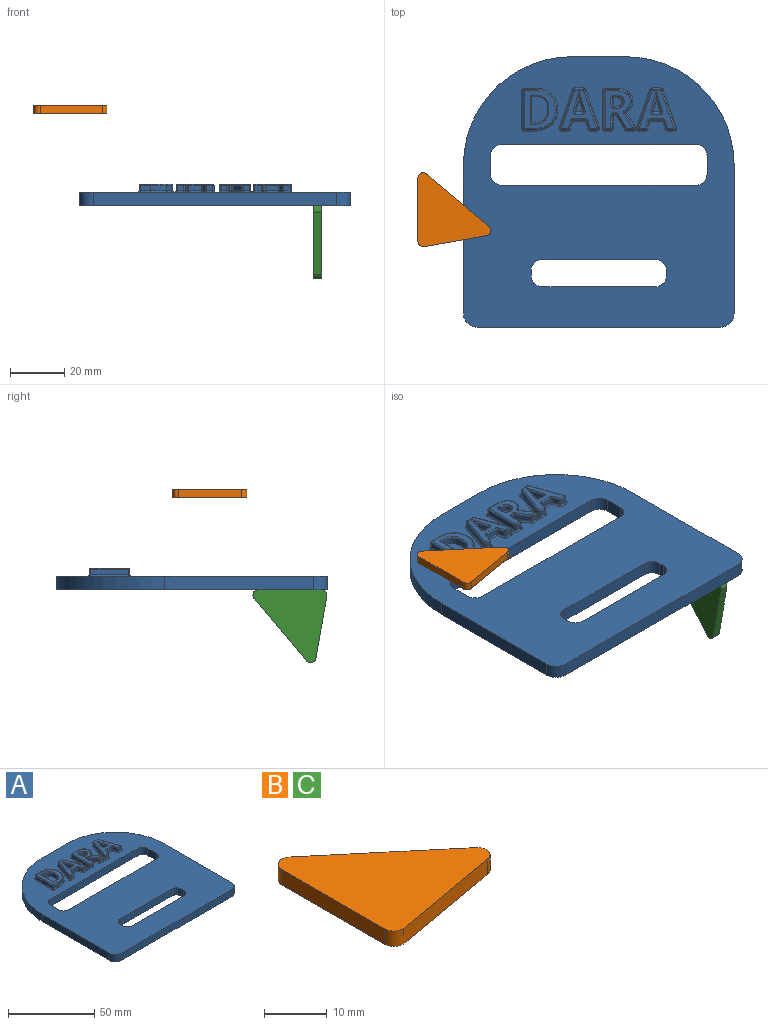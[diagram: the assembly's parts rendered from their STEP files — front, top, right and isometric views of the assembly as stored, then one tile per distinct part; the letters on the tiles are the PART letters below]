
ASSEMBLY  parts=3 mates=1
PART A: 298 faces, bbox 100x100x8 mm
  f0: plane 100x100mm, normal (0,0,1), area 7009.5mm2, adj f1,f2,f3,f4,f5,f6,f7,f8
  f1: plane 20x5mm, normal (0,1,0), area 100mm2, adj f0,f2,f24,f25
  f2: cylinder r=40mm len=40mm, axis (0,0,-1), area 314.2mm2, adj f0,f1,f3,f25
  f3: plane 55x5mm, normal (-1,0,0), area 275mm2, adj f0,f2,f4,f25
  f4: cylinder r=5mm len=5mm, axis (0,0,-1), area 39.3mm2, adj f0,f3,f5,f25
  f5: plane 90x5mm, normal (0,-1,0), area 450mm2, adj f0,f4,f6,f25
  f6: cylinder r=5mm len=5mm, axis (0,0,-1), area 39.3mm2, adj f0,f5,f7,f25
  f7: plane 55x5mm, normal (1,0,0), area 275mm2, adj f0,f6,f24,f25
  f8: cylinder r=4mm len=5mm, axis (0,0,-1), area 31.4mm2, adj f0,f9,f22,f25
  f9: plane 72x5mm, normal (0,-1,0), area 360mm2, adj f0,f8,f10,f25
  f10: cylinder r=4mm len=5mm, axis (0,0,-1), area 31.4mm2, adj f0,f9,f11,f25
  f11: plane 7x5mm, normal (-1,0,0), area 35mm2, adj f0,f10,f12,f25
  f12: cylinder r=4mm len=5mm, axis (0,0,-1), area 31.4mm2, adj f0,f11,f13,f25
  f13: plane 72x5mm, normal (0,1,0), area 360mm2, adj f0,f12,f14,f25
  f14: cylinder r=4mm len=5mm, axis (0,0,-1), area 31.4mm2, adj f0,f13,f22,f25
  f15: cylinder r=4mm len=5mm, axis (0,0,-1), area 31.4mm2, adj f0,f16,f23,f25
  f16: plane 5x2mm, normal (1,0,0), area 10mm2, adj f0,f15,f17,f25
  f17: cylinder r=4mm len=5mm, axis (0,0,-1), area 31.4mm2, adj f0,f16,f18,f25
  f18: plane 42x5mm, normal (0,-1,0), area 210mm2, adj f0,f17,f19,f25
  f19: cylinder r=4mm len=5mm, axis (0,0,-1), area 31.4mm2, adj f0,f18,f20,f25
  f20: plane 5x2mm, normal (-1,0,0), area 10mm2, adj f0,f19,f21,f25
  f21: cylinder r=4mm len=5mm, axis (0,0,-1), area 31.4mm2, adj f0,f20,f23,f25
  f22: plane 7x5mm, normal (1,0,0), area 35mm2, adj f0,f8,f14,f25
  f23: plane 42x5mm, normal (0,1,0), area 210mm2, adj f0,f15,f21,f25
  f24: cylinder r=40mm len=40mm, axis (0,0,-1), area 314.2mm2, adj f0,f1,f7,f25
  f25: plane 100x100mm, normal (0,0,-1), area 7630mm2, adj f1,f2,f3,f4,f5,f6,f7,f8
  f26: extruded ~4.79x4.23mm, area 18.3mm2, adj f27,f37,f39,f112
  f27: extruded ~4.89x4.56mm, area 19.2mm2, adj f26,f28,f39,f113
  f28: plane 2.5x1.35mm, normal (0,1,0), area 3.4mm2, adj f27,f29,f39,f111
  f29: plane 9.68x2.5mm, normal (1,0,0), area 24.2mm2, adj f28,f37,f39,f109
  f30: extruded ~5.63x2.09mm, area 12.4mm2, adj f31,f36,f91,f108
  f31: extruded ~5.37x2.02mm, area 11.8mm2, adj f30,f32,f89,f106
  f32: extruded ~5.66x2mm, area 12.3mm2, adj f31,f33,f90,f104
  f33: plane 4.17x2mm, normal (0,1,0), area 8.3mm2, adj f32,f92,f97,f102
  f34: plane 13.87x2mm, normal (-1,0,0), area 27.7mm2, adj f95,f97,f100,f101
  f35: plane 3.71x2mm, normal (0,-1,0), area 7.4mm2, adj f36,f96,f101,f105
  f36: extruded ~6.04x2mm, area 13mm2, adj f30,f35,f93,f107
  f37: plane 2.5x1.68mm, normal (0,-1,0), area 4.2mm2, adj f26,f29,f39,f110
  f38: plane 13.87x11.34mm, normal (0,0,1), area 74.5mm2, adj f89,f90,f91,f92,f93,f95,f96,f109
  f39: plane 9.68x5.91mm, normal (0,0,1), area 50.1mm2, adj f26,f27,f28,f29,f37
  f40: extruded ~4.79x2mm, area 10mm2, adj f51,f115,f119,f132
  f41: plane 2.52x2mm, normal (0,1,0), area 5mm2, adj f118,f119,f124,f130
  f42: extruded ~5.42x2mm, area 11.3mm2, adj f117,f124,f139,f295
  f43: plane 2.83x2mm, normal (-0.96,-0.29,0), area 5.9mm2, adj f141,f142,f150,f151
  f44: plane 2.32x2mm, normal (0,-1,0), area 4.6mm2, adj f126,f127,f140,f141
  f45: plane 13.94x4.92mm, normal (0.94,0.33,0), area 29.6mm2, adj f120,f126,f129,f131
  f46: plane 3.15x2mm, normal (0,1,0), area 6.3mm2, adj f128,f129,f144,f145
  f47: plane 13.94x4.9mm, normal (-0.94,0.33,0), area 29.5mm2, adj f143,f144,f155,f156
  f48: plane 2.32x2mm, normal (0,-1,0), area 4.6mm2, adj f154,f155,f163,f164
  f49: plane 2.83x2mm, normal (0.96,-0.29,0), area 5.9mm2, adj f153,f162,f163,f167
  f50: plane 4.68x2mm, normal (0,-1,0), area 9.4mm2, adj f151,f152,f161,f162
  f51: extruded ~2x0.62mm, area 1.3mm2, adj f40,f114,f138,f295
  f52: plane 13.94x12.96mm, normal (0,0,1), area 65.1mm2, adj f123,f130,f131,f132,f133,f138,f139,f140
  f53: plane 4.11x2.52mm, normal (0,0,1), area 5.2mm2, adj f115,f117,f118
  f54: plane 4.71x2mm, normal (1,0,0), area 9.4mm2, adj f181,f182,f192,f193
  f55: plane 2x0.9mm, normal (0,-1,0), area 1.8mm2, adj f171,f172,f180,f181
  f56: plane 5.23x3.26mm, normal (-0.85,-0.53,0), area 12.3mm2, adj f168,f171,f174,f175
  f57: plane 2.27x2mm, normal (0,-1,0), area 4.5mm2, adj f173,f174,f185,f186
  f58: extruded ~5.23x3.52mm, area 12.6mm2, adj f184,f185,f196,f197
  f59: extruded ~2x1.55mm, area 4.2mm2, adj f60,f183,f196,f206
  f60: extruded ~2.33x2mm, area 5mm2, adj f59,f61,f189,f209
  f61: extruded ~3.35x2mm, area 7.6mm2, adj f60,f62,f195,f212
  f62: extruded ~4.49x2mm, area 9.4mm2, adj f61,f63,f200,f214
  f63: plane 3.83x2mm, normal (0,1,0), area 7.7mm2, adj f62,f205,f211,f215
  f64: plane 13.87x2mm, normal (-1,0,0), area 27.7mm2, adj f203,f204,f210,f211
  f65: plane 2x0.52mm, normal (0,1,0), area 1mm2, adj f71,f222,f230,f235
  f66: plane 3.02x2mm, normal (1,0,0), area 6mm2, adj f223,f224,f230,f231
  f67: plane 2x0.46mm, normal (0,-1,0), area 0.9mm2, adj f68,f219,f224,f225
  f68: extruded ~2.25x2mm, area 4.6mm2, adj f67,f69,f217,f226
  f69: extruded ~2x1.51mm, area 3.5mm2, adj f68,f70,f216,f229
  f70: extruded ~2x1.57mm, area 3.6mm2, adj f69,f71,f218,f232
  f71: extruded ~2.21x2mm, area 4.6mm2, adj f65,f70,f220,f234
  f72: plane 2.15x2mm, normal (0,-1,0), area 4.3mm2, adj f193,f194,f202,f203
  f73: plane 13.87x10.43mm, normal (0,0,1), area 71.3mm2, adj f175,f176,f180,f186,f187,f192,f197,f201
  f74: plane 3.02x2.94mm, normal (0,0,1), area 7.8mm2, adj f225,f226,f229,f231,f232,f234,f235
  f75: extruded ~4.79x2mm, area 10mm2, adj f86,f265,f277,f283
  f76: plane 2.52x2mm, normal (0,1,0), area 5mm2, adj f272,f277,f284,f285
  f77: extruded ~5.42x2mm, area 11.3mm2, adj f271,f284,f289,f291
  f78: plane 2.83x2mm, normal (-0.96,-0.29,0), area 5.9mm2, adj f241,f242,f252,f253
  f79: plane 2.32x2mm, normal (0,-1,0), area 4.6mm2, adj f251,f252,f263,f266
  f80: plane 13.94x4.92mm, normal (0.94,0.33,0), area 29.6mm2, adj f262,f263,f276,f279
  f81: plane 3.15x2mm, normal (0,1,0), area 6.3mm2, adj f261,f275,f276,f286
  f82: plane 13.94x4.9mm, normal (-0.94,0.33,0), area 29.5mm2, adj f259,f260,f274,f275
  f83: plane 2.32x2mm, normal (0,-1,0), area 4.6mm2, adj f249,f250,f258,f259
  f84: plane 2.83x2mm, normal (0.96,-0.29,0), area 5.9mm2, adj f239,f240,f248,f249
  f85: plane 4.68x2mm, normal (0,-1,0), area 9.4mm2, adj f236,f239,f242,f243
  f86: extruded ~2x0.62mm, area 1.3mm2, adj f75,f264,f287,f291
  f87: plane 13.94x12.96mm, normal (0,0,1), area 65.1mm2, adj f243,f244,f247,f248,f253,f258,f266,f274
  f88: plane 4.11x2.52mm, normal (0,0,1), area 5.2mm2, adj f265,f271,f272
  f89: bspline ~7.66x2.55mm, area 4.5mm2, adj f31,f38,f90,f91
  f90: bspline ~8.89x3.1mm, area 4.7mm2, adj f32,f38,f89,f92
  f91: bspline ~8.55x3.23mm, area 4.7mm2, adj f30,f38,f89,f93
  f92: cylinder r=0.5mm len=4.17mm, axis (1,0,0), area 3.3mm2, adj f33,f38,f90,f94
  f93: bspline ~9.58x3.2mm, area 5mm2, adj f36,f38,f91,f96
  f94: sphere r=0.5mm, area 0.5mm2, adj f92,f95,f97
  f95: cylinder r=0.5mm len=13.87mm, axis (0,1,0), area 10.9mm2, adj f34,f38,f94,f98
  f96: cylinder r=0.5mm len=3.71mm, axis (-1,0,0), area 2.9mm2, adj f35,f38,f93,f98
  f97: cylinder r=0.5mm len=2mm, axis (0,0,-1), area 1.6mm2, adj f33,f34,f94,f99
  f98: sphere r=0.5mm, area 0.4mm2, adj f95,f96,f101
  f99: torus R=1mm, axis (0,0,1), area 0.8mm2, adj f0,f97,f100,f102
  f100: cylinder r=0.5mm len=13.87mm, axis (0,-1,0), area 10.9mm2, adj f0,f34,f99,f103
  f101: cylinder r=0.5mm len=2mm, axis (0,0,-1), area 1.6mm2, adj f34,f35,f98,f103
  f102: cylinder r=0.5mm len=4.17mm, axis (-1,0,0), area 3.3mm2, adj f0,f33,f99,f104
  f103: torus R=1mm, axis (0,0,1), area 0.8mm2, adj f0,f100,f101,f105
  f104: bspline ~9.23x3.24mm, area 4.9mm2, adj f0,f32,f102,f106
  f105: cylinder r=0.5mm len=3.71mm, axis (1,0,0), area 2.9mm2, adj f0,f35,f103,f107
  f106: bspline ~8.56x3.27mm, area 4.8mm2, adj f0,f31,f104,f108
  f107: bspline ~9.92x3.34mm, area 5.2mm2, adj f0,f36,f105,f108
  f108: bspline ~8.91x3.39mm, area 5mm2, adj f0,f30,f106,f107
  f109: cylinder r=0.5mm len=10.68mm, axis (0,-1,0), area 8mm2, adj f29,f38,f110,f111
  f110: cylinder r=0.5mm len=2.18mm, axis (-1,0,0), area 1.5mm2, adj f37,f38,f109,f112
  f111: cylinder r=0.5mm len=1.85mm, axis (1,0,0), area 1.3mm2, adj f28,f38,f109,f113
  f112: bspline ~7.11x6.55mm, area 6mm2, adj f26,f38,f110,f113
  f113: bspline ~7.29x6.96mm, area 6.2mm2, adj f27,f38,f111,f112
  f114: bspline ~1.05x0.74mm, area 0.1mm2, adj f51,f115,f296
  f115: bspline ~6.36x2.4mm, area 3.8mm2, adj f40,f53,f114,f116,f297
  f116: sphere r=0.5mm, area 0.3mm2, adj f115,f118,f119
  f117: bspline ~6.47x2.38mm, area 4mm2, adj f42,f53,f122,f296,f297
  f118: cylinder r=0.5mm len=2.52mm, axis (-1,0,0), area 2mm2, adj f41,f53,f116,f122
  f119: cylinder r=0.5mm len=2mm, axis (0,0,-1), area 1.9mm2, adj f40,f41,f116,f123
  f120: cylinder r=0.5mm len=14.1mm, axis (-0.33,0.94,0), area 11.6mm2, adj f0,f45,f121,f125
  f121: torus R=1mm, axis (0,0,1), area 1mm2, adj f0,f120,f126,f127
  f122: sphere r=0.5mm, area 0.3mm2, adj f117,f118,f124
  f123: torus R=1mm, axis (0,0,1), area 1mm2, adj f52,f119,f130,f132
  f124: cylinder r=0.5mm len=2mm, axis (0,0,-1), area 1.9mm2, adj f41,f42,f122,f133
  f125: torus R=1mm, axis (0,0,1), area 0.7mm2, adj f0,f120,f128,f129
  f126: cylinder r=0.5mm len=2mm, axis (0,0,-1), area 1.9mm2, adj f44,f45,f121,f134
  f127: cylinder r=0.5mm len=2.32mm, axis (1,0,0), area 1.8mm2, adj f0,f44,f121,f135
  f128: cylinder r=0.5mm len=3.15mm, axis (-1,0,0), area 2.5mm2, adj f0,f46,f125,f136
  f129: cylinder r=0.5mm len=2mm, axis (0,0,-1), area 1.2mm2, adj f45,f46,f125,f137
  f130: cylinder r=0.5mm len=2.52mm, axis (1,0,0), area 2mm2, adj f41,f52,f123,f133
  f131: cylinder r=0.5mm len=14.1mm, axis (0.33,-0.94,0), area 11.6mm2, adj f45,f52,f134,f137
  f132: bspline ~5.62x2.17mm, area 3.9mm2, adj f40,f52,f123,f138
  f133: torus R=1mm, axis (0,0,1), area 1mm2, adj f52,f124,f130,f139
  f134: sphere r=0.5mm, area 0.5mm2, adj f126,f131,f140
  f135: torus R=1mm, axis (0,0,1), area 0.7mm2, adj f0,f127,f141,f142
  f136: torus R=1mm, axis (0,0,1), area 0.7mm2, adj f0,f128,f143,f144
  f137: sphere r=0.5mm, area 0.5mm2, adj f129,f131,f145
  f138: bspline ~3.77x1.37mm, area 1.2mm2, adj f51,f52,f132,f145,f294
  f139: bspline ~10.95x3.53mm, area 5.1mm2, adj f42,f52,f133,f145,f294
  f140: cylinder r=0.5mm len=2.32mm, axis (-1,0,0), area 1.8mm2, adj f44,f52,f134,f146
  f141: cylinder r=0.5mm len=2mm, axis (0,0,-1), area 1.3mm2, adj f43,f44,f135,f146
  f142: cylinder r=0.5mm len=2.98mm, axis (0.29,-0.96,0), area 2.3mm2, adj f0,f43,f135,f147
  f143: cylinder r=0.5mm len=14.1mm, axis (-0.33,-0.94,0), area 11.6mm2, adj f0,f47,f136,f148
  f144: cylinder r=0.5mm len=2mm, axis (0,0,-1), area 1.2mm2, adj f46,f47,f136,f149
  f145: cylinder r=0.5mm len=3.15mm, axis (1,0,0), area 2.5mm2, adj f46,f52,f137,f138,f139,f149,f294
  f146: sphere r=0.5mm, area 0.3mm2, adj f140,f141,f150
  f147: sphere r=0.5mm, area 0.2mm2, adj f142,f151,f152
  f148: torus R=1mm, axis (0,0,1), area 1mm2, adj f0,f143,f154,f155
  f149: sphere r=0.5mm, area 0.5mm2, adj f144,f145,f156
  f150: cylinder r=0.5mm len=2.98mm, axis (-0.29,0.96,0), area 2.3mm2, adj f43,f52,f146,f157
  f151: cylinder r=0.5mm len=2mm, axis (0,0,1), area 1.3mm2, adj f43,f50,f147,f157
  f152: cylinder r=0.5mm len=4.68mm, axis (1,0,0), area 3.7mm2, adj f0,f50,f147,f158
  f153: cylinder r=0.5mm len=2.98mm, axis (0.29,0.96,0), area 2.3mm2, adj f0,f49,f158,f159
  f154: cylinder r=0.5mm len=2.32mm, axis (1,0,0), area 1.8mm2, adj f0,f48,f148,f159
  f155: cylinder r=0.5mm len=2mm, axis (0,0,-1), area 1.9mm2, adj f47,f48,f148,f160
  f156: cylinder r=0.5mm len=14.1mm, axis (0.33,0.94,0), area 11.6mm2, adj f47,f52,f149,f160
  f157: torus R=1mm, axis (0,0,1), area 0.7mm2, adj f52,f150,f151,f161
  f158: sphere r=0.5mm, area 0.5mm2, adj f152,f153,f162
  f159: torus R=1mm, axis (0,0,1), area 0.7mm2, adj f0,f153,f154,f163
  f160: sphere r=0.5mm, area 0.5mm2, adj f155,f156,f164
  f161: cylinder r=0.5mm len=4.68mm, axis (-1,0,0), area 3.7mm2, adj f50,f52,f157,f165
  f162: cylinder r=0.5mm len=2mm, axis (0,0,1), area 1.3mm2, adj f49,f50,f158,f165
  f163: cylinder r=0.5mm len=2mm, axis (0,0,-1), area 1.3mm2, adj f48,f49,f159,f166
  f164: cylinder r=0.5mm len=2.32mm, axis (-1,0,0), area 1.8mm2, adj f48,f52,f160,f166
  f165: torus R=1mm, axis (0,0,1), area 0.7mm2, adj f52,f161,f162,f167
  f166: sphere r=0.5mm, area 0.3mm2, adj f163,f164,f167
  f167: cylinder r=0.5mm len=2.98mm, axis (-0.29,-0.96,0), area 2.3mm2, adj f49,f52,f165,f166
  f168: cylinder r=0.5mm len=5.5mm, axis (0.53,-0.85,0), area 4.8mm2, adj f0,f56,f169,f170
  f169: sphere r=0.5mm, area 0.3mm2, adj f168,f171,f172
  f170: torus R=1mm, axis (0,0,1), area 0.5mm2, adj f0,f168,f173,f174
  f171: cylinder r=0.5mm len=2mm, axis (0,0,1), area 1mm2, adj f55,f56,f169,f176
  f172: cylinder r=0.5mm len=0.9mm, axis (1,0,0), area 0.7mm2, adj f0,f55,f169,f177
  f173: cylinder r=0.5mm len=2.27mm, axis (1,0,0), area 1.8mm2, adj f0,f57,f170,f178
  f174: cylinder r=0.5mm len=2mm, axis (0,0,-1), area 1mm2, adj f56,f57,f170,f179
  f175: cylinder r=0.5mm len=5.5mm, axis (-0.53,0.85,0), area 4.8mm2, adj f56,f73,f176,f179
  f176: torus R=1mm, axis (0,0,1), area 0.5mm2, adj f73,f171,f175,f180
  f177: sphere r=0.5mm, area 0.5mm2, adj f172,f181,f182
  f178: torus R=1mm, axis (0,0,1), area 1.2mm2, adj f0,f173,f184,f185
  f179: sphere r=0.5mm, area 0.3mm2, adj f174,f175,f186
  f180: cylinder r=0.5mm len=0.9mm, axis (-1,0,0), area 0.7mm2, adj f55,f73,f176,f187
  f181: cylinder r=0.5mm len=2mm, axis (0,0,1), area 1.6mm2, adj f54,f55,f177,f187
  f182: cylinder r=0.5mm len=4.71mm, axis (0,1,0), area 3.7mm2, adj f0,f54,f177,f188
  f183: bspline ~2.25x2.04mm, area 1.7mm2, adj f0,f59,f189,f190
  f184: bspline ~6.67x4.73mm, area 4.9mm2, adj f0,f58,f178,f190
  f185: cylinder r=0.5mm len=2mm, axis (0,0,-1), area 2.2mm2, adj f57,f58,f178,f191
  f186: cylinder r=0.5mm len=2.27mm, axis (-1,0,0), area 1.8mm2, adj f57,f73,f179,f191
  f187: torus R=1mm, axis (0,0,1), area 0.8mm2, adj f73,f180,f181,f192
  f188: torus R=1mm, axis (0,0,1), area 0.8mm2, adj f0,f182,f193,f194
  f189: bspline ~3.52x1.51mm, area 2mm2, adj f0,f60,f183,f195
  f190: sphere r=0.5mm, area 0.5mm2, adj f183,f184,f196
  f191: sphere r=0.5mm, area 0.5mm2, adj f185,f186,f197
  f192: cylinder r=0.5mm len=4.71mm, axis (0,-1,0), area 3.7mm2, adj f54,f73,f187,f198
  f193: cylinder r=0.5mm len=2mm, axis (0,0,-1), area 1.6mm2, adj f54,f72,f188,f198
  f194: cylinder r=0.5mm len=2.15mm, axis (1,0,0), area 1.7mm2, adj f0,f72,f188,f199
  f195: bspline ~4.18x2.16mm, area 3.1mm2, adj f0,f61,f189,f200
  f196: cylinder r=0.5mm len=2mm, axis (0,0,-1), area 1.7mm2, adj f58,f59,f190,f201
  f197: bspline ~6.75x4.77mm, area 4.9mm2, adj f58,f73,f191,f201
  f198: sphere r=0.5mm, area 0.4mm2, adj f192,f193,f202
  f199: torus R=1mm, axis (0,0,1), area 0.8mm2, adj f0,f194,f203,f204
  f200: bspline ~6.73x2.26mm, area 3.8mm2, adj f0,f62,f195,f205
  f201: torus R=1mm, axis (0,0,1), area 0.9mm2, adj f73,f196,f197,f206
  f202: cylinder r=0.5mm len=2.15mm, axis (-1,0,0), area 1.7mm2, adj f72,f73,f198,f207
  f203: cylinder r=0.5mm len=2mm, axis (0,0,-1), area 1.6mm2, adj f64,f72,f199,f207
  f204: cylinder r=0.5mm len=13.87mm, axis (0,-1,0), area 10.9mm2, adj f0,f64,f199,f208
  f205: cylinder r=0.5mm len=3.83mm, axis (-1,0,0), area 3mm2, adj f0,f63,f200,f208
  f206: bspline ~2.3x2.26mm, area 1.6mm2, adj f59,f73,f201,f209
  f207: sphere r=0.5mm, area 0.4mm2, adj f202,f203,f210
  f208: torus R=1mm, axis (0,0,1), area 0.8mm2, adj f0,f204,f205,f211
  f209: bspline ~3.23x1.41mm, area 1.9mm2, adj f60,f73,f206,f212
  f210: cylinder r=0.5mm len=13.87mm, axis (0,1,0), area 10.9mm2, adj f64,f73,f207,f213
  f211: cylinder r=0.5mm len=2mm, axis (0,0,-1), area 1.6mm2, adj f63,f64,f208,f213
  f212: bspline ~5.08x2.61mm, area 2.9mm2, adj f61,f73,f209,f214
  f213: sphere r=0.5mm, area 0.5mm2, adj f210,f211,f215
  f214: bspline ~6.43x2.15mm, area 3.6mm2, adj f62,f73,f212,f215
  f215: cylinder r=0.5mm len=3.83mm, axis (1,0,0), area 3mm2, adj f63,f73,f213,f214
  f216: bspline ~2.79x1.52mm, area 1.5mm2, adj f69,f73,f217,f218
  f217: bspline ~3.56x1.24mm, area 1.9mm2, adj f68,f73,f216,f219
  f218: bspline ~2.59x1.53mm, area 1.5mm2, adj f70,f73,f216,f220
  f219: cylinder r=0.5mm len=0.5mm, axis (-1,0,0), area 0.4mm2, adj f67,f73,f217,f221
  f220: bspline ~3.52x1.32mm, area 1.9mm2, adj f71,f73,f218,f222
  f221: torus R=1mm, axis (0,0,1), area 0.8mm2, adj f73,f219,f223,f224
  f222: cylinder r=0.5mm len=0.52mm, axis (1,0,0), area 0.4mm2, adj f65,f73,f220,f227
  f223: cylinder r=0.5mm len=3.02mm, axis (0,-1,0), area 2.4mm2, adj f66,f73,f221,f227
  f224: cylinder r=0.5mm len=2mm, axis (0,0,1), area 1.6mm2, adj f66,f67,f221,f228
  f225: cylinder r=0.5mm len=0.5mm, axis (1,0,0), area 0.4mm2, adj f67,f74,f226,f228
  f226: bspline ~3.3x1.17mm, area 1.7mm2, adj f68,f74,f225,f229
  f227: torus R=1mm, axis (0,0,1), area 0.8mm2, adj f73,f222,f223,f230
  f228: sphere r=0.5mm, area 0.5mm2, adj f224,f225,f231
  f229: bspline ~2.36x1.28mm, area 1.2mm2, adj f69,f74,f226,f232
  f230: cylinder r=0.5mm len=2mm, axis (0,0,1), area 1.6mm2, adj f65,f66,f227,f233
  f231: cylinder r=0.5mm len=3.02mm, axis (0,1,0), area 2.4mm2, adj f66,f74,f228,f233
  f232: bspline ~1.9x1.32mm, area 1.3mm2, adj f70,f74,f229,f234
  f233: sphere r=0.5mm, area 0.4mm2, adj f230,f231,f235
  f234: bspline ~2.91x0.99mm, area 1.7mm2, adj f71,f74,f232,f235
  f235: cylinder r=0.5mm len=0.52mm, axis (-1,0,0), area 0.4mm2, adj f65,f74,f233,f234
  f236: cylinder r=0.5mm len=4.68mm, axis (1,0,0), area 3.7mm2, adj f0,f85,f237,f238
  f237: sphere r=0.5mm, area 0.5mm2, adj f236,f239,f240
  f238: sphere r=0.5mm, area 0.2mm2, adj f236,f241,f242
  f239: cylinder r=0.5mm len=2mm, axis (0,0,1), area 1.3mm2, adj f84,f85,f237,f244
  f240: cylinder r=0.5mm len=2.98mm, axis (0.29,0.96,0), area 2.3mm2, adj f0,f84,f237,f245
  f241: cylinder r=0.5mm len=2.98mm, axis (0.29,-0.96,0), area 2.3mm2, adj f0,f78,f238,f246
  f242: cylinder r=0.5mm len=2mm, axis (0,0,1), area 1.3mm2, adj f78,f85,f238,f247
  f243: cylinder r=0.5mm len=4.68mm, axis (-1,0,0), area 3.7mm2, adj f85,f87,f244,f247
  f244: torus R=1mm, axis (0,0,1), area 0.7mm2, adj f87,f239,f243,f248
  f245: torus R=1mm, axis (0,0,1), area 0.7mm2, adj f0,f240,f249,f250
  f246: torus R=1mm, axis (0,0,1), area 0.7mm2, adj f0,f241,f251,f252
  f247: torus R=1mm, axis (0,0,1), area 0.7mm2, adj f87,f242,f243,f253
  f248: cylinder r=0.5mm len=2.98mm, axis (-0.29,-0.96,0), area 2.3mm2, adj f84,f87,f244,f254
  f249: cylinder r=0.5mm len=2mm, axis (0,0,-1), area 1.3mm2, adj f83,f84,f245,f254
  f250: cylinder r=0.5mm len=2.32mm, axis (1,0,0), area 1.8mm2, adj f0,f83,f245,f255
  f251: cylinder r=0.5mm len=2.32mm, axis (1,0,0), area 1.8mm2, adj f0,f79,f246,f256
  f252: cylinder r=0.5mm len=2mm, axis (0,0,-1), area 1.3mm2, adj f78,f79,f246,f257
  f253: cylinder r=0.5mm len=2.98mm, axis (-0.29,0.96,0), area 2.3mm2, adj f78,f87,f247,f257
  f254: sphere r=0.5mm, area 0.3mm2, adj f248,f249,f258
  f255: torus R=1mm, axis (0,0,1), area 1mm2, adj f0,f250,f259,f260
  f256: torus R=1mm, axis (0,0,1), area 1mm2, adj f0,f251,f262,f263
  f257: sphere r=0.5mm, area 0.3mm2, adj f252,f253,f266
  f258: cylinder r=0.5mm len=2.32mm, axis (-1,0,0), area 1.8mm2, adj f83,f87,f254,f267
  f259: cylinder r=0.5mm len=2mm, axis (0,0,-1), area 1.9mm2, adj f82,f83,f255,f267
  f260: cylinder r=0.5mm len=14.1mm, axis (-0.33,-0.94,0), area 11.6mm2, adj f0,f82,f255,f268
  f261: cylinder r=0.5mm len=3.15mm, axis (-1,0,0), area 2.5mm2, adj f0,f81,f268,f269
  f262: cylinder r=0.5mm len=14.1mm, axis (-0.33,0.94,0), area 11.6mm2, adj f0,f80,f256,f269
  f263: cylinder r=0.5mm len=2mm, axis (0,0,-1), area 1.9mm2, adj f79,f80,f256,f273
  f264: bspline ~1.05x0.74mm, area 0.1mm2, adj f86,f265,f292
  f265: bspline ~6.36x2.4mm, area 3.8mm2, adj f75,f88,f264,f270,f293
  f266: cylinder r=0.5mm len=2.32mm, axis (-1,0,0), area 1.8mm2, adj f79,f87,f257,f273
  f267: sphere r=0.5mm, area 0.5mm2, adj f258,f259,f274
  f268: torus R=1mm, axis (0,0,1), area 0.7mm2, adj f0,f260,f261,f275
  f269: torus R=1mm, axis (0,0,1), area 0.7mm2, adj f0,f261,f262,f276
  f270: sphere r=0.5mm, area 0.3mm2, adj f265,f272,f277
  f271: bspline ~6.47x2.38mm, area 4mm2, adj f77,f88,f278,f292,f293
  f272: cylinder r=0.5mm len=2.52mm, axis (-1,0,0), area 2mm2, adj f76,f88,f270,f278
  f273: sphere r=0.5mm, area 0.5mm2, adj f263,f266,f279
  f274: cylinder r=0.5mm len=14.1mm, axis (0.33,0.94,0), area 11.6mm2, adj f82,f87,f267,f281
  f275: cylinder r=0.5mm len=2mm, axis (0,0,-1), area 1.2mm2, adj f81,f82,f268,f281
  f276: cylinder r=0.5mm len=2mm, axis (0,0,-1), area 1.2mm2, adj f80,f81,f269,f282
  f277: cylinder r=0.5mm len=2mm, axis (0,0,-1), area 1.9mm2, adj f75,f76,f270,f280
  f278: sphere r=0.5mm, area 0.5mm2, adj f271,f272,f284
  f279: cylinder r=0.5mm len=14.1mm, axis (0.33,-0.94,0), area 11.6mm2, adj f80,f87,f273,f282
  f280: torus R=1mm, axis (0,0,1), area 1mm2, adj f87,f277,f283,f285
  f281: sphere r=0.5mm, area 0.5mm2, adj f274,f275,f286
  f282: sphere r=0.5mm, area 0.2mm2, adj f276,f279,f286
  f283: bspline ~5.62x2.17mm, area 3.9mm2, adj f75,f87,f280,f287
  f284: cylinder r=0.5mm len=2mm, axis (0,0,-1), area 1.9mm2, adj f76,f77,f278,f288
  f285: cylinder r=0.5mm len=2.52mm, axis (1,0,0), area 2mm2, adj f76,f87,f280,f288
  f286: cylinder r=0.5mm len=3.15mm, axis (1,0,0), area 2.5mm2, adj f81,f87,f281,f282,f287,f289,f290
  f287: bspline ~3.77x1.37mm, area 1.2mm2, adj f86,f87,f283,f286,f290
  f288: torus R=1mm, axis (0,0,1), area 1mm2, adj f87,f284,f285,f289
  f289: bspline ~10.95x3.53mm, area 5.1mm2, adj f77,f87,f286,f288,f290
  f290: bspline ~2.51x0.58mm, area 0.3mm2, adj f286,f287,f289,f291
  f291: cylinder r=0.1mm len=2mm, axis (0,0,-1), area 0.5mm2, adj f77,f86,f290,f292
  f292: bspline ~1.18x0.52mm, area 0.2mm2, adj f264,f271,f291,f293
  f293: bspline ~0.95x0.13mm, area 0mm2, adj f265,f271,f292
  f294: bspline ~2.51x0.58mm, area 0.3mm2, adj f138,f139,f145,f295
  f295: cylinder r=0.1mm len=2mm, axis (0,0,-1), area 0.5mm2, adj f42,f51,f294,f296
  f296: bspline ~1.18x0.52mm, area 0.2mm2, adj f114,f117,f295,f297
  f297: bspline ~0.95x0.13mm, area 0mm2, adj f115,f117,f296
PART B: 8 faces, bbox 27x27.3x3 mm
  f0: plane 23.33x3mm, normal (-1,0,0), area 70mm2, adj f3,f4,f5,f7
  f1: plane 22.97x4.05mm, normal (0.17,-0.98,0), area 70mm2, adj f3,f4,f5,f6
  f2: plane 22.97x19.28mm, normal (0.64,0.77,0), area 90mm2, adj f3,f4,f6,f7
  f3: plane 27.33x26.97mm, normal (0,0,1), area 433.8mm2, adj f0,f1,f2,f5,f6,f7
  f4: plane 27.33x26.97mm, normal (0,0,-1), area 433.8mm2, adj f0,f1,f2,f5,f6,f7
  f5: cylinder r=2mm len=3mm, axis (0,0,-1), area 10.5mm2, adj f0,f1,f3,f4
  f6: cylinder r=2mm len=3.5mm, axis (0,0,-1), area 13.6mm2, adj f1,f2,f3,f4
  f7: cylinder r=2mm len=3.29mm, axis (0,0,-1), area 13.6mm2, adj f0,f2,f3,f4
PART C: same geometry as B
PLACE A at identity fixed
PLACE B t=(-66.83,-20.65,34.1)mm
PLACE C rot(axis=(-0.54,-0.64,0.54),114.4deg) t=(39.35,-50.24,0)mm
MATE planar A.f25 <-> C.f1  axis (0,0,-1) through (-21,-25,0)mm
